# Revit family: MBH1
name_source: partatom
category: Lighting Fixtures
units: mm (PartAtom-declared; Revit-internal decimal feet)

## family parameters
Always vertical = Yes
Cut with Voids When Loaded = No
Host = Ceiling
Light Source = Yes
OmniClass Number = 23.80.70.11.14.17
OmniClass Title = Direct/Indirect
Part Type = Normal
Room Calculation Point = No
Round Connector Dimension = Use Diameter
Shared = No

## types (4) — shared parameters
Assembly Code = D5020200
Color Filter = 16777215
Description = LED Medical 1 Recessed Patient Room
Diffuser Finish = Polycarbonate - Viscor - Frosted Formed
Dimming Lamp Color Temperature Shift = <None>
Emit Shape Visible in Rendering = No
Emit from Rectangle Width = 1' - 11 3/4"
Housing Finish = Metal - Viscor - White
Lamp = LED
Lens Finish = Polycarbonate - Viscor - Clear Flat Smooth Lens
Manufacturer = CERTOLUX by VISCOR
Model = MD1U Patient Room
Tilt Angle = 90.00°
URL = https://www.viscor.com
Voltage = 120 V
Width = 1' - 11 3/4"

## per-type parameters (varying)
| type | Apparent Load | Emit from Rectangle Length | Lamp Wattage | Length | Photometric Web File |
| MBH1x2X2-LED840K30LUNV-C84G-P08 | 27 VA | 1' - 11 3/4" | 27 VA | 1' - 11 3/4" | MBH1x2X2-LED840K30LUNV-C84G-P08.ies |
| MBH1x2X4-LED840K45_80LUNV-C84G-P08 | 113 VA | 3' - 11 3/4" | 113 VA | 3' - 11 3/4" | MBH1x2X4-LED840K45_80LUNV-C84G-P08.ies |
| MBH1x2X2-LED840K30_60LUNV-C84G-P08 | 79 VA | 1' - 11 3/4" | 79 VA | 1' - 11 3/4" | MBH1x2X2-LED840K30_60LUNV-C84G-P08.ies |
| MBH1x2X4-LED840K45LUNV-C84G-P08 | 40 VA | 3' - 11 3/4" | 40 VA | 3' - 11 3/4" | MBH1x2X4-LED840K45LUNV-C84G-P08.ies |

## geometry (parser evidence)
native form markers: Sweep x2
no freeform markers — native parametric forms only
